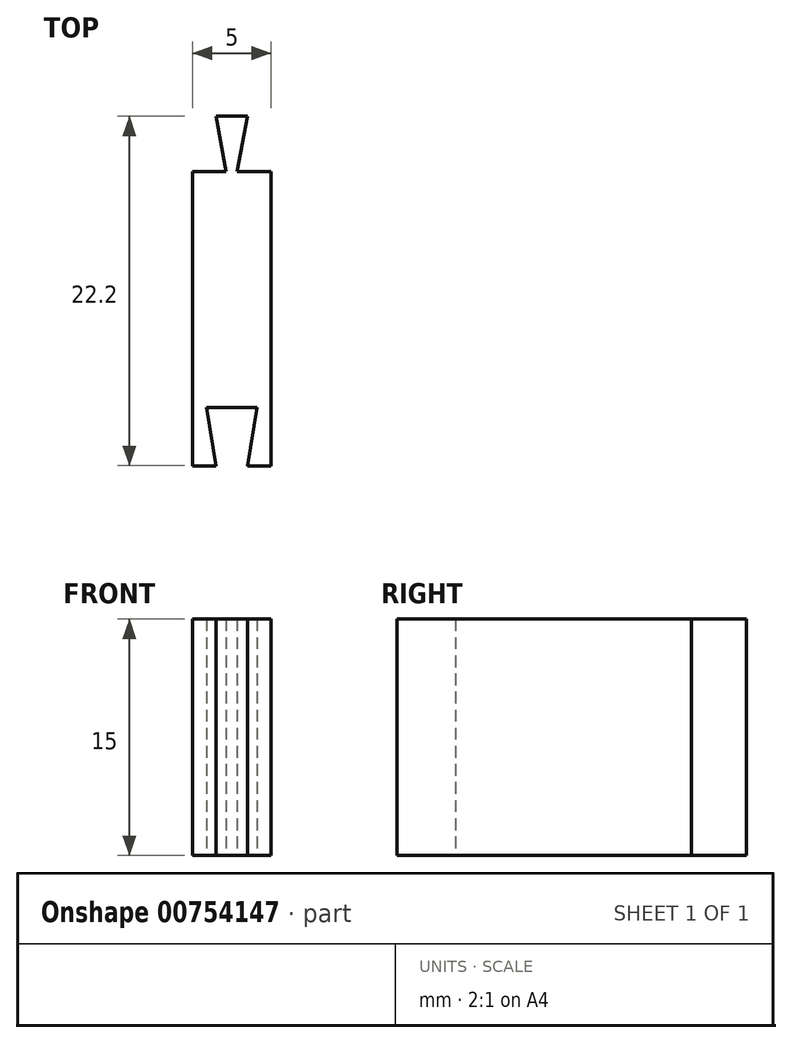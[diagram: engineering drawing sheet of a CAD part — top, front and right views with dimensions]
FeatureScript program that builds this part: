
annotation { "Feature Type Name" : "Feature", "Feature Type Description" : "" }
export const myFeature = defineFeature(function(context is Context, id is Id, definition is map)
    precondition{}
    {
        {
            var Q0;
            Q0=qCreatedBy(makeId("Top.planeOp"),FACE);
            var sketch = newSketch(context, id + "F0", { "sketchPlane" : qUnion([Q0])});
            skLineSegment(sketch, "E0", {"start": v(-72.93, 10.76) * mm, "end": v(-72.93, -4.24) * mm});
            skLineSegment(sketch, "E1", {"start": v(-72.93, -4.24) * mm, "end": v(-67.93, -4.24) * mm});
            skLineSegment(sketch, "E2", {"start": v(-67.93, -4.24) * mm, "end": v(-67.93, 10.76) * mm});
            skLineSegment(sketch, "E3", {"start": v(-67.93, 10.76) * mm, "end": v(-72.93, 10.76) * mm});
            skLineSegment(sketch, "E4", {"start": v(-72.93, 10.76) * mm, "end": v(-72.93, 14.26) * mm});
            skLineSegment(sketch, "E5", {"start": v(-72.93, 14.26) * mm, "end": v(-67.93, 14.26) * mm});
            skLineSegment(sketch, "E6", {"start": v(-67.93, 14.26) * mm, "end": v(-67.93, 10.76) * mm});
            skLineSegment(sketch, "E7", {"start": v(-72.93, -4.24) * mm, "end": v(-72.93, -7.94) * mm});
            skLineSegment(sketch, "E8", {"start": v(-72.93, -7.94) * mm, "end": v(-67.93, -7.94) * mm});
            skLineSegment(sketch, "E9", {"start": v(-67.93, -7.94) * mm, "end": v(-67.93, -4.24) * mm});
            skLineSegment(sketch, "E10", {"start": v(-70.43, 14.26) * mm, "end": v(-70.43, 10.76) * mm, "construction": true});
            skLineSegment(sketch, "E11", {"start": v(-71.43, 14.26) * mm, "end": v(-70.78, 10.76) * mm});
            skLineSegment(sketch, "E12.MirrorCS", {"start": v(-69.43, 14.26) * mm, "end": v(-70.08, 10.76) * mm});
            skLineSegment(sketch, "E13", {"start": v(-70.43, -4.24) * mm, "end": v(-70.43, -7.94) * mm, "construction": true});
            skLineSegment(sketch, "E14", {"start": v(-72.03, -4.24) * mm, "end": v(-71.43, -7.94) * mm});
            skLineSegment(sketch, "E15.MirrorCS", {"start": v(-68.83, -4.24) * mm, "end": v(-69.43, -7.94) * mm});
            skSolve(sketch);
        }
        {
            var Q0;
            {var subQ4=sQuery(id+"F0.wireOp",EDGE,"E0");Q0=makeQuery(id+"F0.imprint","IMPRINT",FACE,{"disambiguationData":[TD([[makeQuery(id+"F0.imprint","IMPRINT",EDGE,{"derivedFrom":subQ4}),1.0]])]});}
            var Q1;
            {var subQ0=sQuery(id+"F0.wireOp",EDGE,"E11");Q1=makeQuery(id+"F0.imprint","IMPRINT",FACE,{"disambiguationData":[TD([[makeQuery(id+"F0.imprint","IMPRINT",EDGE,{"derivedFrom":subQ0}),1.0]])]});}
            var Q2;
            {var subQ0=sQuery(id+"F0.wireOp",EDGE,"E7");Q2=makeQuery(id+"F0.imprint","IMPRINT",FACE,{"disambiguationData":[TD([[makeQuery(id+"F0.imprint","IMPRINT",EDGE,{"derivedFrom":subQ0}),1.0]])]});}
            var Q3;
            {var subQ0=sQuery(id+"F0.wireOp",EDGE,"E9");Q3=makeQuery(id+"F0.imprint","IMPRINT",FACE,{"disambiguationData":[TD([[makeQuery(id+"F0.imprint","IMPRINT",EDGE,{"derivedFrom":subQ0}),1.0]])]});}
            extrude(context, id + "F1", {"entities" : qUnion([Q0, Q1, Q2, Q3]), "depth" : 15 * mm, "offsetDistance" : 25 * mm});
        }
    });
